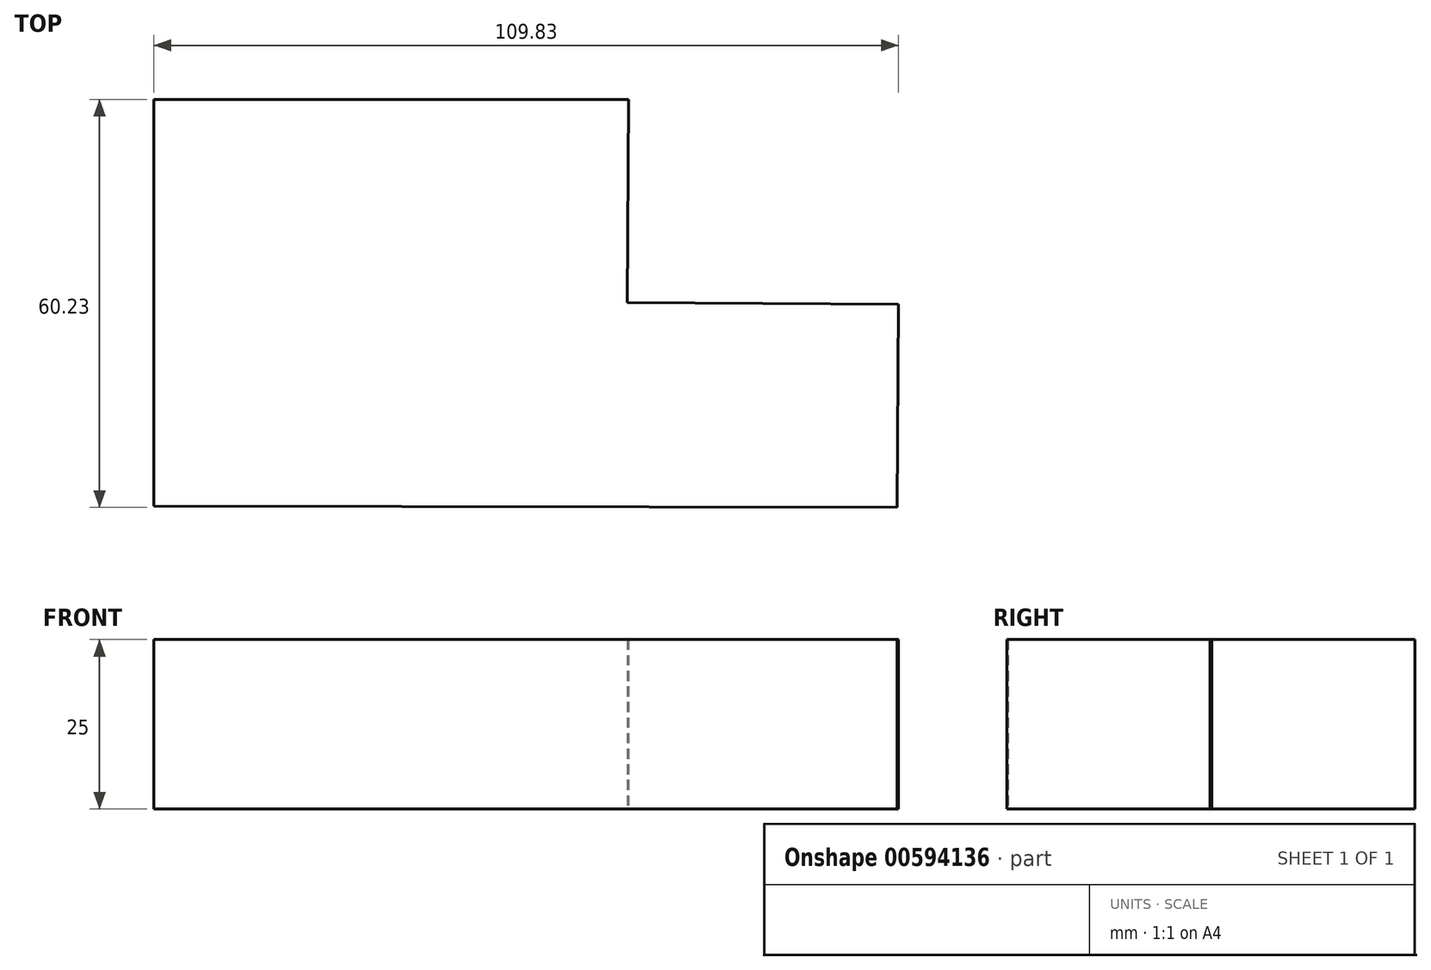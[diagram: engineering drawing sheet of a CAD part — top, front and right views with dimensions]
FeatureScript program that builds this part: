
annotation { "Feature Type Name" : "Feature", "Feature Type Description" : "" }
export const myFeature = defineFeature(function(context is Context, id is Id, definition is map)
    precondition{}
    {
        {
            var Q0;
            Q0=qCreatedBy(makeId("Top.planeOp"),FACE);
            var sketch = newSketch(context, id + "F0", { "sketchPlane" : qUnion([Q0])});
            skLineSegment(sketch, "E0", {"start": v(-55.11, -4.91) * mm, "end": v(-55.11, 55.09) * mm});
            skLineSegment(sketch, "E1", {"start": v(-55.11, 55.09) * mm, "end": v(14.89, 55.09) * mm});
            skLineSegment(sketch, "E2", {"start": v(14.89, 55.09) * mm, "end": v(14.72, 25.09) * mm});
            skLineSegment(sketch, "E3", {"start": v(14.72, 25.09) * mm, "end": v(54.72, 24.86) * mm});
            skLineSegment(sketch, "E4", {"start": v(54.72, 24.86) * mm, "end": v(54.55, -5.14) * mm});
            skLineSegment(sketch, "E5", {"start": v(54.55, -5.14) * mm, "end": v(-55.11, -4.91) * mm});
            skSolve(sketch);
        }
        {
            var Q0;
            Q0=makeQuery(id+"F0.imprint","IMPRINT",FACE,{"disambiguationData":[TD([[makeQuery(id+"F0.imprint","IMPRINT",EDGE,{"derivedFrom":sQuery(id+"F0.wireOp",EDGE,"E0")}),-1.0]])]});
            extrude(context, id + "F1", {"entities" : qUnion([Q0]), "depth" : 25 * mm, "offsetDistance" : 25 * mm});
        }
    });
